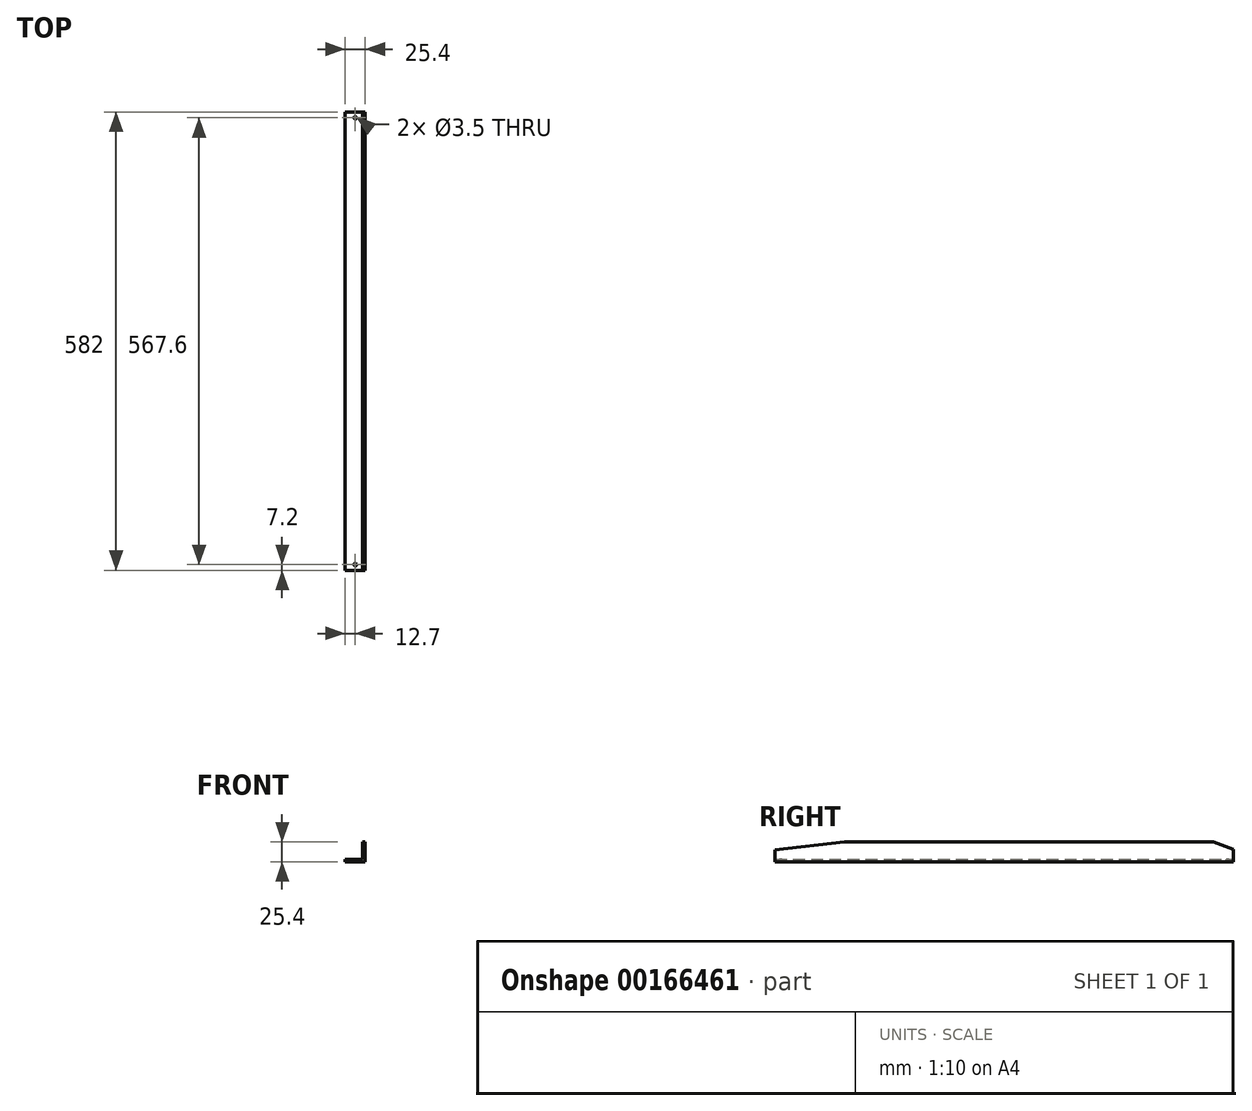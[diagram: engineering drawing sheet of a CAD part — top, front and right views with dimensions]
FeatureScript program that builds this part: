
annotation { "Feature Type Name" : "Feature", "Feature Type Description" : "" }
export const myFeature = defineFeature(function(context is Context, id is Id, definition is map)
    precondition{}
    {
        {
            var Q0;
            Q0=qCreatedBy(makeId("Front.planeOp"),FACE);
            var sketch = newSketch(context, id + "F0", { "sketchPlane" : qUnion([Q0])});
            skLineSegment(sketch, "E0.bottom", {"start": v(22.2, 12.7) * mm, "end": v(25.4, 12.7) * mm});
            skLineSegment(sketch, "E0.top", {"start": v(0, -12.7) * mm, "end": v(25.4, -12.7) * mm});
            skLineSegment(sketch, "E0.right", {"start": v(25.4, 12.7) * mm, "end": v(25.4, -12.7) * mm});
            skPoint(sketch, "E0.middle", {"position": v(0, 0) * mm});
            skLineSegment(sketch, "E1", {"start": v(0, -9.5) * mm, "end": v(0, -12.7) * mm});
            skPoint(sketch, "E1.endSnap0", {"position": v(0, -12.7) * mm});
            skLineSegment(sketch, "E2", {"start": v(0, -9.5) * mm, "end": v(22.2, -9.5) * mm});
            skLineSegment(sketch, "E3", {"start": v(22.2, -9.5) * mm, "end": v(22.2, 12.7) * mm});
            skPoint(sketch, "E0.left.end.orphan", {"position": v(-25.4, -12.7) * mm});
            skPoint(sketch, "E4.orphan", {"position": v(-25.4, 12.7) * mm});
            skSolve(sketch);
        }
        {
            var Q0;
            Q0 = qSketchRegion(id + "F0", true);
            extrude(context, id + "F1", {"entities" : qUnion([Q0]), "endBound" : BoundingType.SYMMETRIC, "depth" : 582 * mm});
        }
        {
            var Q0;
            Q0=makeQuery(id+"F1.opExtrude","CAP_FACE",FACE,{"disambiguationData":[OSD([sQuery(id+"F0.wireOp",EDGE,"E0.bottom"),sQuery(id+"F0.wireOp",EDGE,"E0.top"),sQuery(id+"F0.wireOp",EDGE,"E0.right"),sQuery(id+"F0.wireOp",EDGE,"E1"),sQuery(id+"F0.wireOp",EDGE,"E2"),sQuery(id+"F0.wireOp",EDGE,"E3")])],"isStart":false});
            var sketch = newSketch(context, id + "F2", { "sketchPlane" : qUnion([Q0])});
            skLineSegment(sketch, "E5.bottom", {"start": v(22.2, 12.7) * mm, "end": v(25.4, 12.7) * mm});
            skLineSegment(sketch, "E5.top", {"start": v(22.2, 7.7) * mm, "end": v(25.4, 7.7) * mm});
            skLineSegment(sketch, "E5.left", {"start": v(22.2, 12.7) * mm, "end": v(22.2, 7.7) * mm});
            skLineSegment(sketch, "E5.right", {"start": v(25.4, 12.7) * mm, "end": v(25.4, 7.7) * mm});
            skSolve(sketch);
        }
        {
            var Q0;
            Q0=makeQuery(id+"F1.opExtrude","CAP_EDGE",EDGE,{"disambiguationData":[OSD([sQuery(id+"F0.wireOp",EDGE,"E0.bottom")])],"isStart":true});
            chamfer(context, id + "F3", {"entities" : qUnion([Q0]), "chamferType" : ChamferType.TWO_OFFSETS, "width1" : 9.5 * mm, "oppositeDirection" : false, "width2" : 25 * mm, "tangentPropagation" : true});
        }
        {
            var Q0;
            Q0=makeQuery(id+"F1.opExtrude","CAP_EDGE",EDGE,{"disambiguationData":[OSD([sQuery(id+"F0.wireOp",EDGE,"E0.bottom")])],"isStart":false});
            chamfer(context, id + "F4", {"entities" : qUnion([Q0]), "chamferType" : ChamferType.TWO_OFFSETS, "width1" : 88 * mm, "oppositeDirection" : false, "width2" : 10.1 * mm, "tangentPropagation" : true});
        }
        {
            var Q0;
            Q0=makeQuery(id+"F1.opExtrude","SWEPT_FACE",FACE,{"disambiguationData":[OSD([sQuery(id+"F0.wireOp",EDGE,"E2")])]});
            var sketch = newSketch(context, id + "F5", { "sketchPlane" : qUnion([Q0])});
            skSolve(sketch);
        }
        {
            var Q0;
            {var subQ0=sQuery(id+"F0.wireOp",EDGE,"E2");Q0=makeQuery(id+"F5.imprint","IMPRINT",FACE,{"disambiguationData":[TD([[makeQuery(id+"F5.imprint","IMPRINT",EDGE,{"derivedFrom":makeQuery(id+"F1.opExtrude","CAP_EDGE",EDGE,{"disambiguationData":[OSD([subQ0])],"isStart":true})}),-1.0]])]});}
            var sketch = newSketch(context, id + "F6", { "sketchPlane" : qUnion([Q0])});
            skCircle(sketch, "E6", {"center": v(12.7, -283.8) * mm, "radius": 1.75 * mm});
            skCircle(sketch, "E7.MirrorC", {"center": v(12.7, 283.8) * mm, "radius": 1.75 * mm});
            skSolve(sketch);
        }
        {
            var Q0;
            Q0 = qSketchRegion(id + "F6", true);
            extrude(context, id + "F7", {"entities" : qUnion([Q0]), "operationType" : NewBodyOperationType.REMOVE, "endBound" : BoundingType.UP_TO_NEXT, "oppositeDirection" : true, "depth" : 25 * mm});
        }
    });
